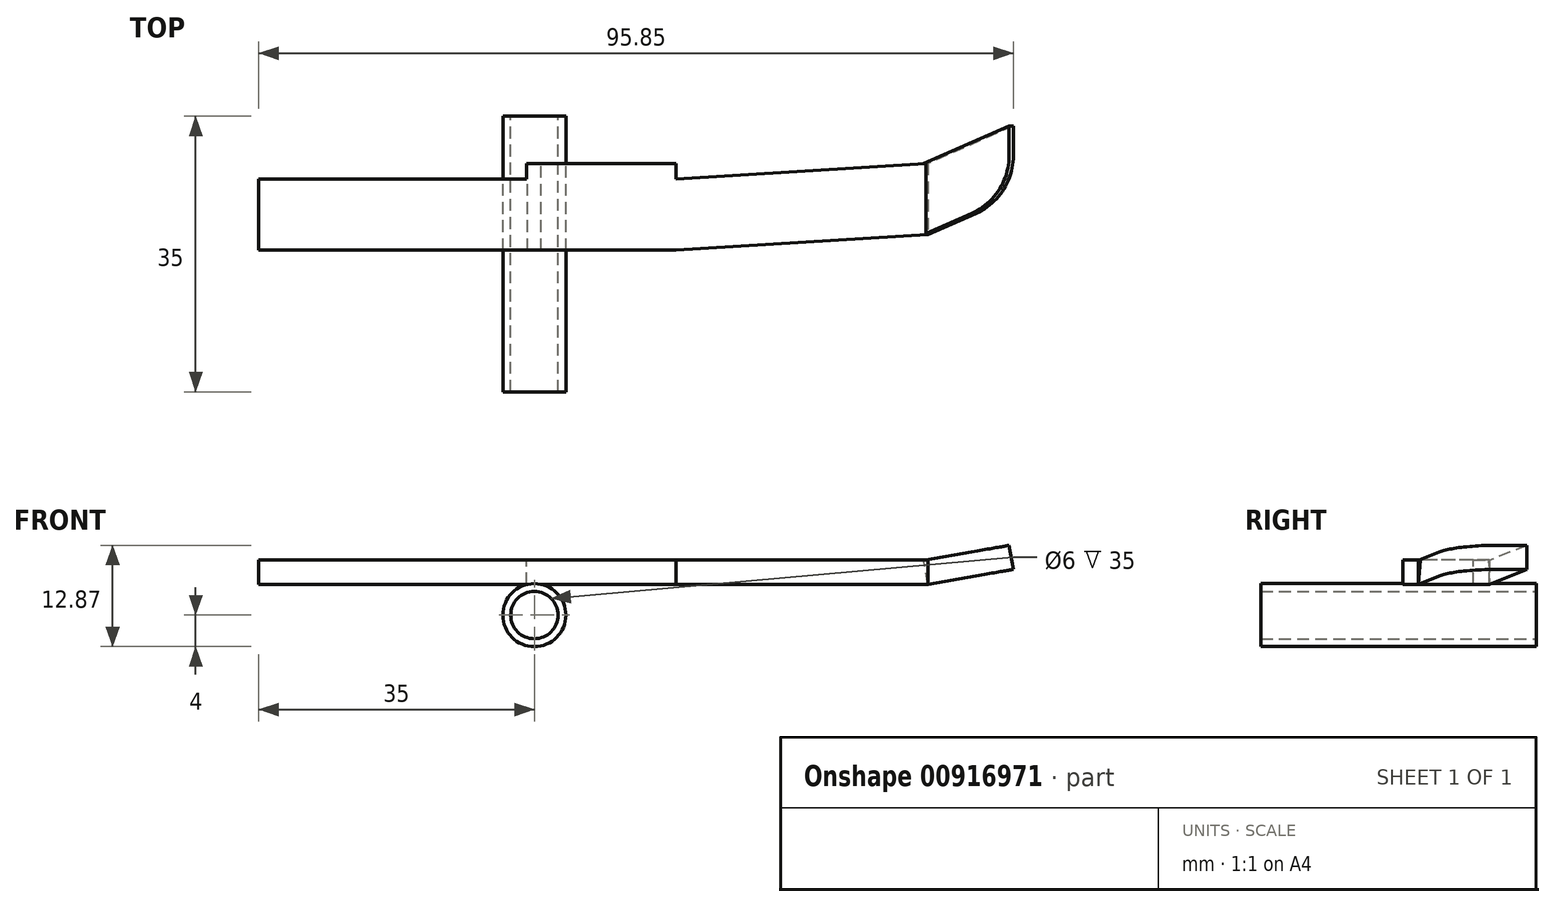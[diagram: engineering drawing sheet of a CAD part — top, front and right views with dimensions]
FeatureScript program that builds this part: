
annotation { "Feature Type Name" : "Feature", "Feature Type Description" : "" }
export const myFeature = defineFeature(function(context is Context, id is Id, definition is map)
    precondition{}
    {
        {
            var Q0;
            Q0=qCreatedBy(makeId("Front.planeOp"),FACE);
            var sketch = newSketch(context, id + "F0", { "sketchPlane" : qUnion([Q0])});
            skCircle(sketch, "E0", {"center": v(0, 0) * mm, "radius": 4 * mm});
            skCircle(sketch, "E1", {"center": v(0, 0) * mm, "radius": 3 * mm});
            skSolve(sketch);
        }
        {
            var Q0;
            Q0 = qSketchRegion(id + "F0", true);
            extrude(context, id + "F1", {"entities" : qUnion([Q0]), "depth" : 35 * mm, "offsetDistance" : 25 * mm});
        }
        {
            var Q0;
            Q0=qCreatedBy(makeId("Front.planeOp"),FACE);
            cPlane(context, id + "F2", {"entities" : qUnion([Q0]), "cplaneType" : CPlaneType.OFFSET, "offset" : 17 * mm, "width" : 150 * mm, "height" : 150 * mm});
        }
        {
            var Q0;
            Q0=qCreatedBy(id+"F2.planeOp",FACE);
            var sketch = newSketch(context, id + "F3", { "sketchPlane" : qUnion([Q0])});
            skLineSegment(sketch, "E2.bottom", {"start": v(-35, 7) * mm, "end": v(50, 7) * mm});
            skLineSegment(sketch, "E2.top", {"start": v(-35, 3.9) * mm, "end": v(50, 3.9) * mm});
            skLineSegment(sketch, "E2.left", {"start": v(-35, 7) * mm, "end": v(-35, 3.9) * mm});
            skLineSegment(sketch, "E2.right", {"start": v(50, 7) * mm, "end": v(50, 3.9) * mm});
            skSolve(sketch);
        }
        {
            var Q0;
            Q0 = qSketchRegion(id + "F3", true);
            extrude(context, id + "F4", {"entities" : qUnion([Q0]), "operationType" : NewBodyOperationType.ADD, "oppositeDirection" : true, "depth" : 11 * mm, "offsetDistance" : 25 * mm});
        }
        {
            var Q0;
            Q0=makeQuery(id+"F4.opExtrude","SWEPT_FACE",FACE,{"disambiguationData":[OSD([sQuery(id+"F3.wireOp",EDGE,"E2.bottom")])]});
            var sketch = newSketch(context, id + "F5", { "sketchPlane" : qUnion([Q0])});
            skLineSegment(sketch, "E3.bottom", {"start": v(-35, -6) * mm, "end": v(-1, -6) * mm});
            skLineSegment(sketch, "E3.top", {"start": v(-35, -8) * mm, "end": v(-1, -8) * mm});
            skLineSegment(sketch, "E3.left", {"start": v(-35, -6) * mm, "end": v(-35, -8) * mm});
            skLineSegment(sketch, "E3.right", {"start": v(-1, -6) * mm, "end": v(-1, -8) * mm});
            skLineSegment(sketch, "E4", {"start": v(18, -6) * mm, "end": v(18, -8) * mm});
            skLineSegment(sketch, "E5", {"start": v(18, -8) * mm, "end": v(50, -6) * mm});
            skLineSegment(sketch, "E6", {"start": v(50, -6) * mm, "end": v(18, -6) * mm});
            skLineSegment(sketch, "E7", {"start": v(18, -17) * mm, "end": v(50, -15) * mm});
            skLineSegment(sketch, "E8", {"start": v(50, -15) * mm, "end": v(50, -17) * mm});
            skLineSegment(sketch, "E9", {"start": v(50, -17) * mm, "end": v(18, -17) * mm});
            skSolve(sketch);
        }
        {
            var Q0;
            Q0=makeQuery(id+"F5.imprint","IMPRINT",FACE,{"disambiguationData":[TD([[makeQuery(id+"F5.imprint","IMPRINT",EDGE,{"derivedFrom":sQuery(id+"F5.wireOp",EDGE,"E3.bottom")}),-1.0]])]});
            var Q1;
            Q1=makeQuery(id+"F5.imprint","IMPRINT",FACE,{"disambiguationData":[TD([[makeQuery(id+"F5.imprint","IMPRINT",EDGE,{"derivedFrom":sQuery(id+"F5.wireOp",EDGE,"E4")}),1.0]])]});
            var Q2;
            Q2=makeQuery(id+"F5.imprint","IMPRINT",FACE,{"disambiguationData":[TD([[makeQuery(id+"F5.imprint","IMPRINT",EDGE,{"derivedFrom":sQuery(id+"F5.wireOp",EDGE,"E7")}),-1.0]])]});
            extrude(context, id + "F6", {"entities" : qUnion([Q0, Q1, Q2]), "operationType" : NewBodyOperationType.REMOVE, "oppositeDirection" : true, "depth" : 3.1 * mm, "offsetDistance" : 25 * mm});
        }
        {
            var Q0;
            Q0=makeQuery(id+"F4.opExtrude","SWEPT_EDGE",EDGE,{"disambiguationData":[OSD([sQuery(id+"F3.wireOp",EDGE,"E2.top"),sQuery(id+"F3.wireOp",EDGE,"E2.right")])]});
            cPlane(context, id + "F7", {"entities" : qUnion([Q0]), "cplaneType" : CPlaneType.LINE_ANGLE, "offset" : 25 * mm, "angle" : 10 * degree, "width" : 150 * mm, "height" : 150 * mm});
        }
        {
            var Q0;
            Q0=qCreatedBy(id+"F7.planeOp",FACE);
            var sketch = newSketch(context, id + "F8", { "sketchPlane" : qUnion([Q0])});
            skLineSegment(sketch, "E10", {"start": v(49.92, 15) * mm, "end": v(60.93, 10.24) * mm});
            skLineSegment(sketch, "E11", {"start": v(60.93, 10.24) * mm, "end": v(60.93, 1.24) * mm});
            skLineSegment(sketch, "E12", {"start": v(60.93, 1.24) * mm, "end": v(49.92, 6) * mm});
            skLineSegment(sketch, "E13", {"start": v(49.92, 6) * mm, "end": v(49.92, 15) * mm});
            skSolve(sketch);
        }
        {
            var Q0;
            Q0=makeQuery(id+"F8.imprint","IMPRINT",FACE,{"disambiguationData":[TD([[makeQuery(id+"F8.imprint","IMPRINT",EDGE,{"derivedFrom":sQuery(id+"F8.wireOp",EDGE,"E10")}),-1.0]])]});
            extrude(context, id + "F9", {"entities" : qUnion([Q0]), "operationType" : NewBodyOperationType.ADD, "oppositeDirection" : true, "depth" : 3.1 * mm, "offsetDistance" : 25 * mm});
        }
        {
            var Q0;
            Q0=makeQuery(id+"F9.opExtrude","SWEPT_EDGE",EDGE,{"disambiguationData":[OSD([sQuery(id+"F8.wireOp",EDGE,"E10"),sQuery(id+"F8.wireOp",EDGE,"E11")])]});
            fillet(context, id + "F10", {"entities" : qUnion([Q0]), "radius" : 8 * mm, "tangentPropagation" : true, "allowEdgeOverflow" : false});
        }
    });
